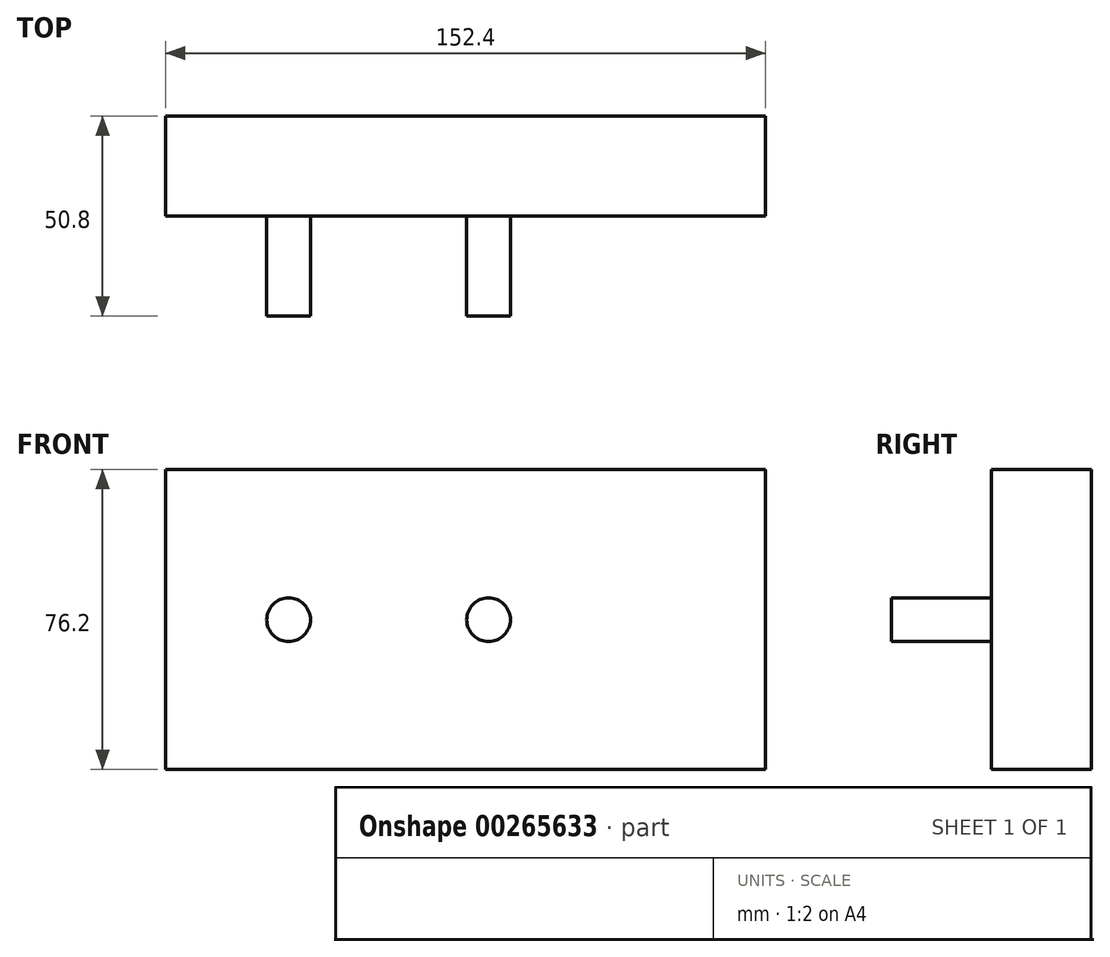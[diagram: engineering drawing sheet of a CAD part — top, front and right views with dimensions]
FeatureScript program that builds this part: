
annotation { "Feature Type Name" : "Feature", "Feature Type Description" : "" }
export const myFeature = defineFeature(function(context is Context, id is Id, definition is map)
    precondition{}
    {
        {
            var Q0;
            Q0=qCreatedBy(makeId("Front.planeOp"),FACE);
            var sketch = newSketch(context, id + "F0", { "sketchPlane" : qUnion([Q0])});
            skLineSegment(sketch, "E0.bottom", {"start": v(0, 0) * mm, "end": v(152.4, 0) * mm});
            skLineSegment(sketch, "E0.top", {"start": v(0, 76.2) * mm, "end": v(152.4, 76.2) * mm});
            skLineSegment(sketch, "E0.left", {"start": v(0, 0) * mm, "end": v(0, 76.2) * mm});
            skLineSegment(sketch, "E0.right", {"start": v(152.4, 0) * mm, "end": v(152.4, 76.2) * mm});
            skSolve(sketch);
        }
        {
            var Q0;
            Q0 = qSketchRegion(id + "F0", true);
            extrude(context, id + "F1", {"entities" : qUnion([Q0]), "depth" : 25.4 * mm});
        }
        {
            var Q0;
            Q0=qCreatedBy(makeId("Front.planeOp"),FACE);
            var sketch = newSketch(context, id + "F2", { "sketchPlane" : qUnion([Q0])});
            skCircle(sketch, "E1", {"center": v(31.24, 38.04) * mm, "radius": 5.56 * mm});
            skLineSegment(sketch, "E2", {"start": v(31.24, 38.04) * mm, "end": v(82.04, 38.04) * mm, "construction": true});
            skCircle(sketch, "E3", {"center": v(82.04, 38.04) * mm, "radius": 5.56 * mm});
            skSolve(sketch);
        }
        {
            var Q0;
            Q0 = qSketchRegion(id + "F2", true);
            extrude(context, id + "F3", {"entities" : qUnion([Q0]), "operationType" : NewBodyOperationType.ADD, "depth" : 50.8 * mm});
        }
    });
